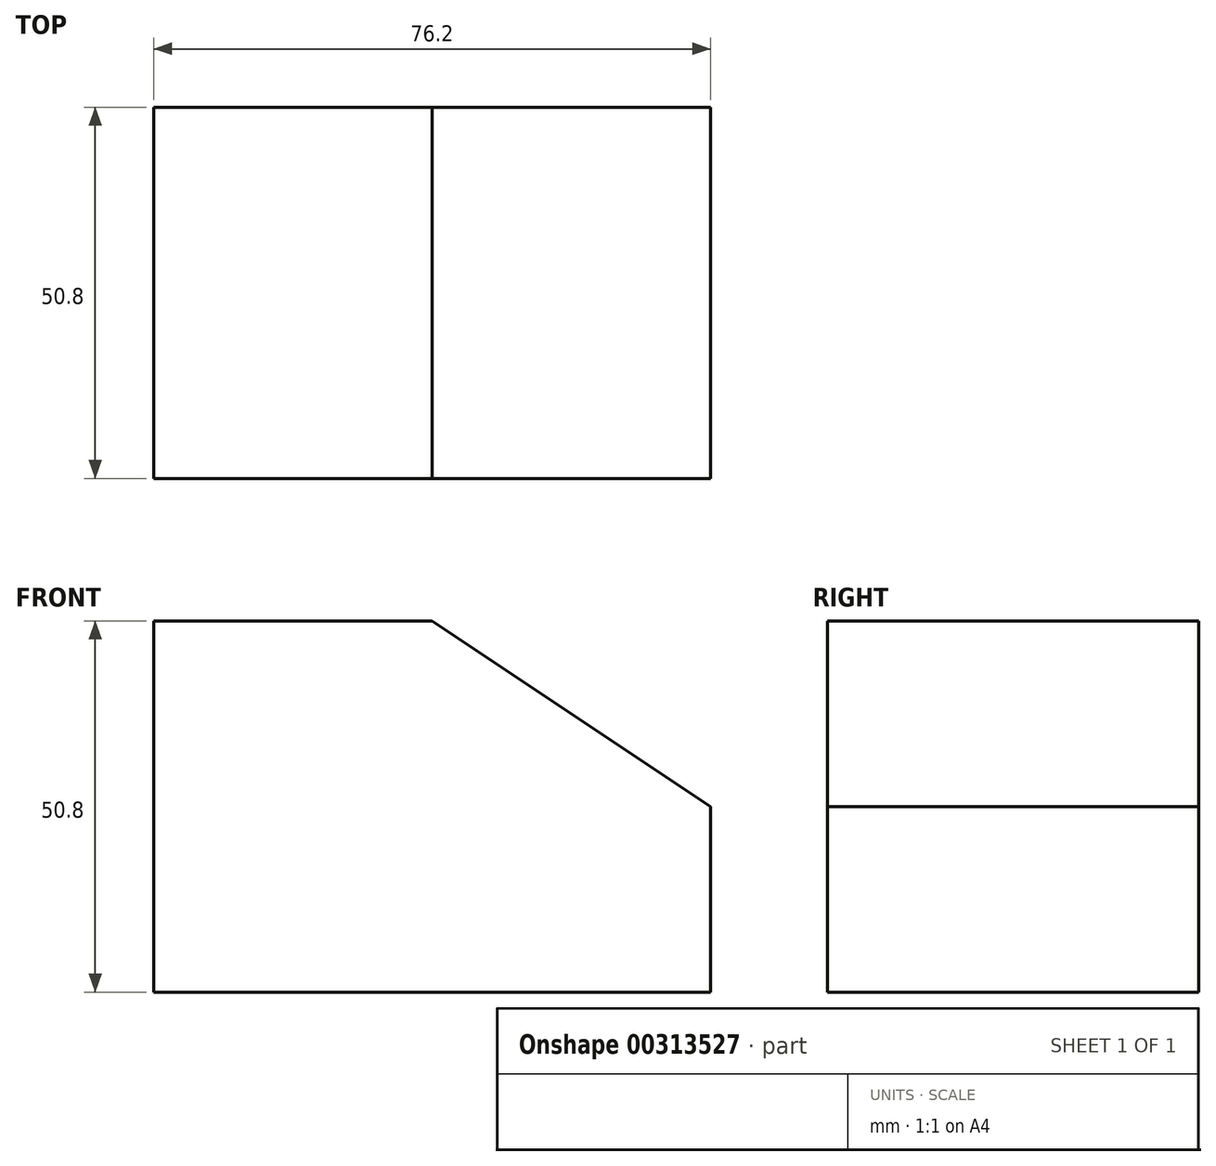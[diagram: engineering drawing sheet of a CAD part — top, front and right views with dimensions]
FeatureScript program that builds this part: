
annotation { "Feature Type Name" : "Feature", "Feature Type Description" : "" }
export const myFeature = defineFeature(function(context is Context, id is Id, definition is map)
    precondition{}
    {
        {
            var Q0;
            Q0=qCreatedBy(makeId("Front.planeOp"),FACE);
            var sketch = newSketch(context, id + "F0", { "sketchPlane" : qUnion([Q0])});
            skLineSegment(sketch, "E0", {"start": v(-42.92, -33.58) * mm, "end": v(33.28, -33.58) * mm});
            skLineSegment(sketch, "E1", {"start": v(33.28, -33.58) * mm, "end": v(33.28, -8.18) * mm});
            skLineSegment(sketch, "E2", {"start": v(33.28, -8.18) * mm, "end": v(-4.82, 17.22) * mm});
            skLineSegment(sketch, "E3", {"start": v(-4.82, 17.22) * mm, "end": v(-42.92, 17.22) * mm});
            skLineSegment(sketch, "E4", {"start": v(-42.92, 17.22) * mm, "end": v(-42.92, -33.58) * mm});
            skSolve(sketch);
        }
        {
            var Q0;
            Q0=makeQuery(id+"F0.imprint","IMPRINT",FACE,{"disambiguationData":[TD([[makeQuery(id+"F0.imprint","IMPRINT",EDGE,{"derivedFrom":sQuery(id+"F0.wireOp",EDGE,"E0")}),1.0]])]});
            extrude(context, id + "F1", {"entities" : qUnion([Q0]), "depth" : 50.8 * mm});
        }
    });
